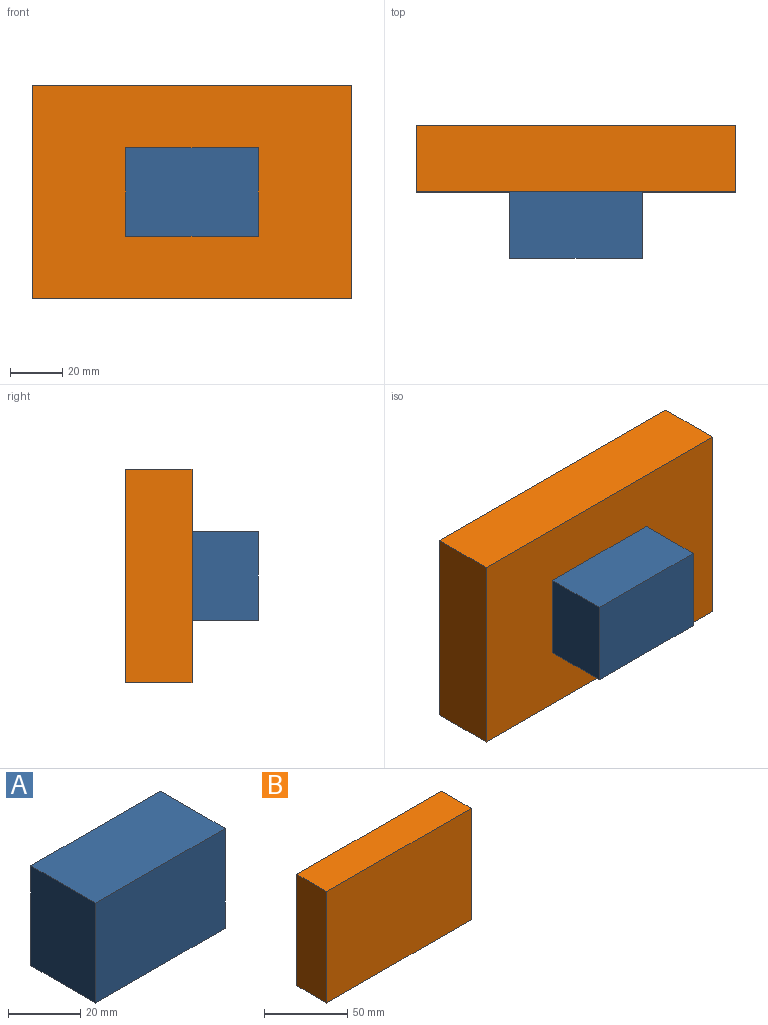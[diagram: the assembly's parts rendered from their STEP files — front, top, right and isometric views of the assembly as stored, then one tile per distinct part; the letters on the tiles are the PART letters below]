
ASSEMBLY  parts=2 mates=1
PART A: 6 faces, bbox 50.8x25.4x33.9 mm
  f0: plane 50.8x25.4mm, normal (0,0,1), area 1290.3mm2, adj f1,f3,f4,f5
  f1: plane 33.91x25.4mm, normal (-1,0,0), area 861.4mm2, adj f0,f2,f4,f5
  f2: plane 50.8x25.4mm, normal (0,0,-1), area 1290.3mm2, adj f1,f3,f4,f5
  f3: plane 33.91x25.4mm, normal (1,0,0), area 861.4mm2, adj f0,f2,f4,f5
  f4: plane 50.8x33.91mm, normal (0,-1,0), area 1722.8mm2, adj f0,f1,f2,f3
  f5: plane 50.8x33.91mm, normal (0,1,0), area 1722.8mm2, adj f0,f1,f2,f3
PART B: 6 faces, bbox 122.6x25.4x81.8 mm
  f0: plane 122.6x25.4mm, normal (0,0,1), area 3114.1mm2, adj f1,f3,f4,f5
  f1: plane 81.85x25.4mm, normal (-1,0,0), area 2078.9mm2, adj f0,f2,f4,f5
  f2: plane 122.6x25.4mm, normal (0,0,-1), area 3114.1mm2, adj f1,f3,f4,f5
  f3: plane 81.85x25.4mm, normal (1,0,0), area 2078.9mm2, adj f0,f2,f4,f5
  f4: plane 122.6x81.85mm, normal (0,-1,0), area 10034.6mm2, adj f0,f1,f2,f3
  f5: plane 122.6x81.85mm, normal (0,1,0), area 10034.6mm2, adj f0,f1,f2,f3
PLACE A t=(-87.29,-54.26,-23.01)mm
PLACE B t=(-87.29,-28.86,-23.01)mm
MATE planar B.f4 <-> A.f5  axis (0,-1,0) through (-93.93,-54.26,-19.1)mm
